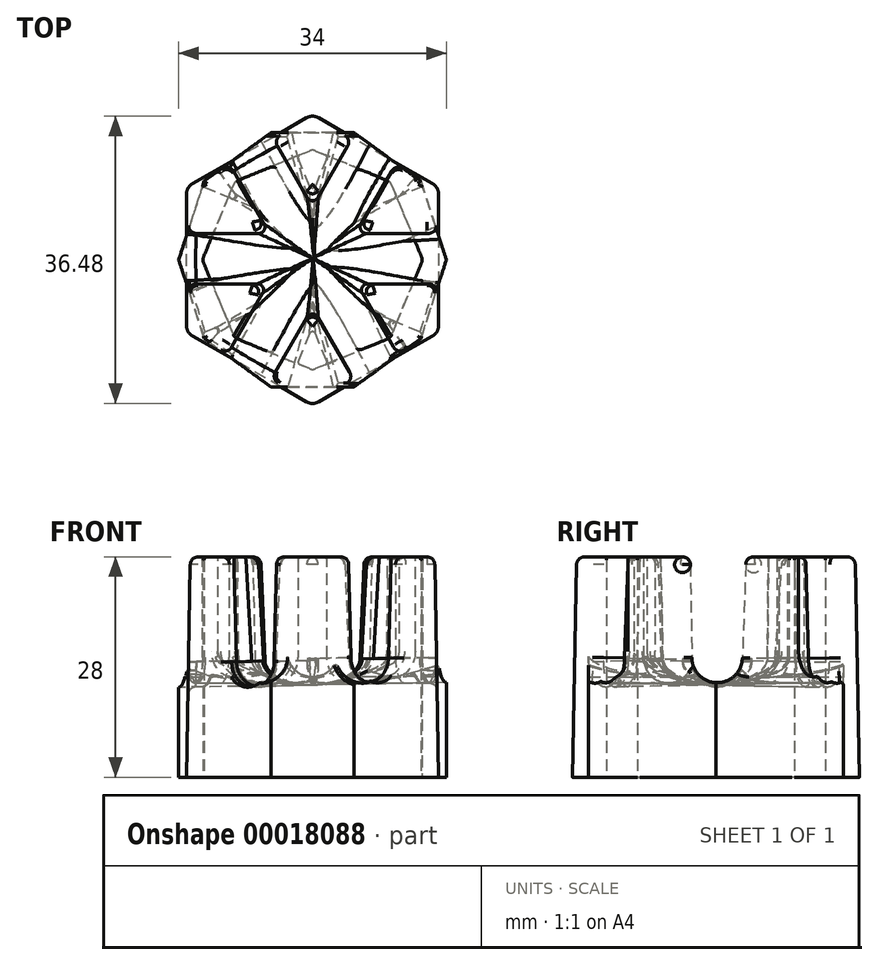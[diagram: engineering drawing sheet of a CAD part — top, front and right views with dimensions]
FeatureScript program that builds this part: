
annotation { "Feature Type Name" : "Feature", "Feature Type Description" : "" }
export const myFeature = defineFeature(function(context is Context, id is Id, definition is map)
    precondition{}
    {
        {
            var Q0;
            Q0=qCreatedBy(makeId("Top.planeOp"),FACE);
            var sketch = newSketch(context, id + "F0", { "sketchPlane" : qUnion([Q0])});
            skCircle(sketch, "E0.cCircle", {"center": v(0, 0) * mm, "radius": 17 * mm, "construction": true});
            skLineSegment(sketch, "E0.0", {"start": v(17, 0) * mm, "end": v(13.75, -10) * mm});
            skLineSegment(sketch, "E0.1", {"start": v(13.75, -10) * mm, "end": v(5.25, -16.17) * mm});
            skLineSegment(sketch, "E0.2", {"start": v(5.25, -16.17) * mm, "end": v(-5.25, -16.17) * mm});
            skLineSegment(sketch, "E0.3", {"start": v(-5.25, -16.17) * mm, "end": v(-13.75, -10) * mm});
            skLineSegment(sketch, "E0.4", {"start": v(-13.75, -10) * mm, "end": v(-17, 0) * mm});
            skLineSegment(sketch, "E0.5", {"start": v(-17, 0) * mm, "end": v(-13.75, 10) * mm});
            skLineSegment(sketch, "E0.6", {"start": v(-13.75, 10) * mm, "end": v(-5.25, 16.17) * mm});
            skLineSegment(sketch, "E0.7", {"start": v(-5.25, 16.17) * mm, "end": v(5.25, 16.17) * mm});
            skLineSegment(sketch, "E0.8", {"start": v(5.25, 16.17) * mm, "end": v(13.75, 10) * mm});
            skLineSegment(sketch, "E0.9", {"start": v(13.75, 10) * mm, "end": v(17, 0) * mm});
            skSolve(sketch);
        }
        {
            var Q0;
            Q0 = qSketchRegion(id + "F0", true);
            extrude(context, id + "F1", {"entities" : qUnion([Q0]), "depth" : 28 * mm});
        }
        {
            var Q0;
            Q0 = qSketchRegion(id + "F0", true);
            extrude(context, id + "F2", {"entities" : qUnion([Q0]), "operationType" : NewBodyOperationType.ADD, "depth" : 25 * mm});
        }
        {
            var Q0;
            Q0=makeQuery(id+"F1.opExtrude","SWEPT_FACE",FACE,{"disambiguationData":[OSD([sQuery(id+"F0.wireOp",EDGE,"E0.2")])]});
            var sketch = newSketch(context, id + "F3", { "sketchPlane" : qUnion([Q0])});
            skArc(sketch, "E1", {"start": v(-3.25, 16) * mm, "mid": v(0, 12.75) * mm, "end": v(3.25, 16) * mm});
            skLineSegment(sketch, "E2", {"start": v(-3.25, 28) * mm, "end": v(-3.25, 16) * mm});
            skLineSegment(sketch, "E3", {"start": v(3.25, 16) * mm, "end": v(3.25, 28) * mm});
            skLineSegment(sketch, "E4", {"start": v(3.25, 28) * mm, "end": v(-3.25, 28) * mm});
            skSolve(sketch);
        }
        {
            var Q0;
            Q0 = qSketchRegion(id + "F3", true);
            extrude(context, id + "F4", {"entities" : qUnion([Q0]), "depth" : 10 * mm, "hasSecondDirection" : true, "secondDirectionOppositeDirection" : true, "secondDirectionDepth" : 40 * mm});
        }
        {
            var Q0;
            Q0=qCreatedBy(makeId("Front.planeOp"),FACE);
            var sketch = newSketch(context, id + "F5", { "sketchPlane" : qUnion([Q0])});
            skLineSegment(sketch, "E5", {"start": v(0, 0) * mm, "end": v(0, 33.77) * mm});
            skSolve(sketch);
        }
        {
            var Q0;
            Q0=makeQuery(id+"F4.opExtrude","SWEPT_BODY",BODY,{"disambiguationData":[OSD([sQuery(id+"F3.wireOp",EDGE,"E1"),sQuery(id+"F3.wireOp",EDGE,"E2"),sQuery(id+"F3.wireOp",EDGE,"E3"),sQuery(id+"F3.wireOp",EDGE,"E4")])]});
            var Q1;
            Q1=sQuery(id+"F5.wireOp",EDGE,"E5");
            circularPattern(context, id + "F6", {"operationType" : NewBodyOperationType.REMOVE, "entities" : qUnion([Q0]), "axis" : qUnion([Q1]), "angle" : 35 * degree, "instanceCount" : 5});
        }
        {
            var Q0;
            Q0=qCreatedBy(makeId("Top.planeOp"),FACE);
            var sketch = newSketch(context, id + "F7", { "sketchPlane" : qUnion([Q0])});
            skCircle(sketch, "E6.cCircle", {"center": v(0, 0) * mm, "radius": 14 * mm, "construction": true});
            skLineSegment(sketch, "E6.0", {"start": v(14, 0) * mm, "end": v(9.9, -9.9) * mm});
            skLineSegment(sketch, "E6.1", {"start": v(9.9, -9.9) * mm, "end": v(0, -14) * mm});
            skLineSegment(sketch, "E6.2", {"start": v(0, -14) * mm, "end": v(-9.9, -9.9) * mm});
            skLineSegment(sketch, "E6.3", {"start": v(-9.9, -9.9) * mm, "end": v(-14, 0) * mm});
            skLineSegment(sketch, "E6.4", {"start": v(-14, 0) * mm, "end": v(-9.9, 9.9) * mm});
            skLineSegment(sketch, "E6.5", {"start": v(-9.9, 9.9) * mm, "end": v(0, 14) * mm});
            skLineSegment(sketch, "E6.6", {"start": v(0, 14) * mm, "end": v(9.9, 9.9) * mm});
            skLineSegment(sketch, "E6.7", {"start": v(9.9, 9.9) * mm, "end": v(14, 0) * mm});
            skSolve(sketch);
        }
        {
            var Q0;
            Q0=makeQuery(id+"F7.imprint","IMPRINT",FACE,{"disambiguationData":[TD([[makeQuery(id+"F7.imprint","IMPRINT",EDGE,{"derivedFrom":sQuery(id+"F7.wireOp",EDGE,"E6.0")}),-1.0]])]});
            extrude(context, id + "F8", {"entities" : qUnion([Q0]), "depth" : 28 * mm});
        }
        {
            var Q0;
            Q0=makeQuery(id+"F8.opExtrude","SWEPT_FACE",FACE,{"disambiguationData":[OSD([sQuery(id+"F7.wireOp",EDGE,"E6.1")])]});
            var sketch = newSketch(context, id + "F9", { "sketchPlane" : qUnion([Q0])});
            skLineSegment(sketch, "E7", {"start": v(0, 28) * mm, "end": v(0, 0) * mm, "construction": true});
            skArc(sketch, "E8", {"start": v(-3.25, 15.2) * mm, "mid": v(0, 11.95) * mm, "end": v(3.25, 15.2) * mm});
            skLineSegment(sketch, "E9", {"start": v(-3.25, 15.2) * mm, "end": v(-3.25, 28) * mm});
            skLineSegment(sketch, "E10", {"start": v(3.25, 15.2) * mm, "end": v(3.25, 28) * mm});
            skLineSegment(sketch, "E11", {"start": v(3.25, 28) * mm, "end": v(-3.25, 28) * mm});
            skSolve(sketch);
        }
        {
            var Q0;
            Q0 = qSketchRegion(id + "F9", true);
            extrude(context, id + "F10", {"entities" : qUnion([Q0]), "depth" : 25 * mm, "hasSecondDirection" : true, "secondDirectionOppositeDirection" : true, "secondDirectionDepth" : 34 * mm});
        }
        {
            var Q0;
            Q0=makeQuery(id+"F10.opExtrude","SWEPT_BODY",BODY,{"disambiguationData":[OSD([sQuery(id+"F9.wireOp",EDGE,"E8"),sQuery(id+"F9.wireOp",EDGE,"E9"),sQuery(id+"F9.wireOp",EDGE,"E10"),sQuery(id+"F9.wireOp",EDGE,"E11")])]});
            var Q1;
            Q1=sQuery(id+"F5.wireOp",EDGE,"E5");
            circularPattern(context, id + "F11", {"operationType" : NewBodyOperationType.REMOVE, "entities" : qUnion([Q0]), "axis" : qUnion([Q1]), "angle" : 45 * degree, "instanceCount" : 4});
        }
        {
            var Q0;
            Q0=makeQuery(id+"F8.opExtrude","SWEPT_EDGE",EDGE,{"disambiguationData":[OSD([sQuery(id+"F7.wireOp",EDGE,"E6.2"),sQuery(id+"F7.wireOp",EDGE,"E6.3")])]});
            var Q1;
            Q1=makeQuery(id+"F8.opExtrude","SWEPT_EDGE",EDGE,{"disambiguationData":[OSD([sQuery(id+"F7.wireOp",EDGE,"E6.1"),sQuery(id+"F7.wireOp",EDGE,"E6.2")])]});
            var Q2;
            Q2=makeQuery(id+"F8.opExtrude","SWEPT_EDGE",EDGE,{"disambiguationData":[OSD([sQuery(id+"F7.wireOp",EDGE,"E6.0"),sQuery(id+"F7.wireOp",EDGE,"E6.1")])]});
            var Q3;
            Q3=makeQuery(id+"F8.opExtrude","SWEPT_EDGE",EDGE,{"disambiguationData":[OSD([sQuery(id+"F7.wireOp",EDGE,"E6.0"),sQuery(id+"F7.wireOp",EDGE,"E6.7")])]});
            var Q4;
            Q4=makeQuery(id+"F8.opExtrude","SWEPT_EDGE",EDGE,{"disambiguationData":[OSD([sQuery(id+"F7.wireOp",EDGE,"E6.6"),sQuery(id+"F7.wireOp",EDGE,"E6.7")])]});
            var Q5;
            Q5=makeQuery(id+"F8.opExtrude","SWEPT_EDGE",EDGE,{"disambiguationData":[OSD([sQuery(id+"F7.wireOp",EDGE,"E6.5"),sQuery(id+"F7.wireOp",EDGE,"E6.6")])]});
            var Q6;
            Q6=makeQuery(id+"F8.opExtrude","SWEPT_EDGE",EDGE,{"disambiguationData":[OSD([sQuery(id+"F7.wireOp",EDGE,"E6.4"),sQuery(id+"F7.wireOp",EDGE,"E6.5")])]});
            var Q7;
            Q7=makeQuery(id+"F8.opExtrude","SWEPT_EDGE",EDGE,{"disambiguationData":[OSD([sQuery(id+"F7.wireOp",EDGE,"E6.3"),sQuery(id+"F7.wireOp",EDGE,"E6.4")])]});
            fillet(context, id + "F12", {"entities" : qUnion([Q0, Q1, Q2, Q3, Q4, Q5, Q6, Q7]), "radius" : 1 * mm, "tangentPropagation" : true, "allowEdgeOverflow" : false});
        }
        {
            var Q0;
            {var subQ0=sQuery(id+"F7.wireOp",EDGE,"E6.0");var subQ1=sQuery(id+"F7.wireOp",EDGE,"E6.1");Q0=makeQuery(id+"F11.boolean.opBoolean","SPLIT",FACE,{"disambiguationData":[TD([makeQuery(id+"F8.opExtrude","SWEPT_FACE",FACE,{"disambiguationData":[OSD([subQ0])]}),makeQuery(id+"F8.opExtrude","SWEPT_FACE",FACE,{"disambiguationData":[OSD([subQ1])]}),makeQuery(id+"F10.opExtrude","SWEPT_FACE",FACE,{"disambiguationData":[OSD([sQuery(id+"F9.wireOp",EDGE,"E10")])]}),makeQuery(id+"F11.opPattern","COPY",FACE,{"derivedFrom":makeQuery(id+"F10.opExtrude","SWEPT_FACE",FACE,{"disambiguationData":[OSD([sQuery(id+"F9.wireOp",EDGE,"E9")])]}),"instanceName":"1"})])],"derivedFrom":makeQuery(id+"F8.opExtrude","CAP_FACE",FACE,{"disambiguationData":[OSD([subQ0,subQ1,sQuery(id+"F7.wireOp",EDGE,"E6.2"),sQuery(id+"F7.wireOp",EDGE,"E6.3"),sQuery(id+"F7.wireOp",EDGE,"E6.4"),sQuery(id+"F7.wireOp",EDGE,"E6.5"),sQuery(id+"F7.wireOp",EDGE,"E6.6"),sQuery(id+"F7.wireOp",EDGE,"E6.7")])],"isStart":false})});}
            var Q1;
            {var subQ0=sQuery(id+"F7.wireOp",EDGE,"E6.0");var subQ1=sQuery(id+"F7.wireOp",EDGE,"E6.7");Q1=makeQuery(id+"F11.boolean.opBoolean","SPLIT",FACE,{"disambiguationData":[TD([makeQuery(id+"F8.opExtrude","SWEPT_FACE",FACE,{"disambiguationData":[OSD([subQ0])]}),makeQuery(id+"F8.opExtrude","SWEPT_FACE",FACE,{"disambiguationData":[OSD([subQ1])]}),makeQuery(id+"F11.opPattern","COPY",FACE,{"derivedFrom":makeQuery(id+"F10.opExtrude","SWEPT_FACE",FACE,{"disambiguationData":[OSD([sQuery(id+"F9.wireOp",EDGE,"E10")])]}),"instanceName":"1"}),makeQuery(id+"F11.opPattern","COPY",FACE,{"derivedFrom":makeQuery(id+"F10.opExtrude","SWEPT_FACE",FACE,{"disambiguationData":[OSD([sQuery(id+"F9.wireOp",EDGE,"E9")])]}),"instanceName":"2"})])],"derivedFrom":makeQuery(id+"F8.opExtrude","CAP_FACE",FACE,{"disambiguationData":[OSD([subQ0,sQuery(id+"F7.wireOp",EDGE,"E6.1"),sQuery(id+"F7.wireOp",EDGE,"E6.2"),sQuery(id+"F7.wireOp",EDGE,"E6.3"),sQuery(id+"F7.wireOp",EDGE,"E6.4"),sQuery(id+"F7.wireOp",EDGE,"E6.5"),sQuery(id+"F7.wireOp",EDGE,"E6.6"),subQ1])],"isStart":false})});}
            var Q2;
            {var subQ0=sQuery(id+"F7.wireOp",EDGE,"E6.6");var subQ1=sQuery(id+"F7.wireOp",EDGE,"E6.7");Q2=makeQuery(id+"F11.boolean.opBoolean","SPLIT",FACE,{"disambiguationData":[TD([makeQuery(id+"F8.opExtrude","SWEPT_FACE",FACE,{"disambiguationData":[OSD([subQ0])]}),makeQuery(id+"F8.opExtrude","SWEPT_FACE",FACE,{"disambiguationData":[OSD([subQ1])]}),makeQuery(id+"F11.opPattern","COPY",FACE,{"derivedFrom":makeQuery(id+"F10.opExtrude","SWEPT_FACE",FACE,{"disambiguationData":[OSD([sQuery(id+"F9.wireOp",EDGE,"E10")])]}),"instanceName":"2"}),makeQuery(id+"F11.opPattern","COPY",FACE,{"derivedFrom":makeQuery(id+"F10.opExtrude","SWEPT_FACE",FACE,{"disambiguationData":[OSD([sQuery(id+"F9.wireOp",EDGE,"E9")])]}),"instanceName":"3"})])],"derivedFrom":makeQuery(id+"F8.opExtrude","CAP_FACE",FACE,{"disambiguationData":[OSD([sQuery(id+"F7.wireOp",EDGE,"E6.0"),sQuery(id+"F7.wireOp",EDGE,"E6.1"),sQuery(id+"F7.wireOp",EDGE,"E6.2"),sQuery(id+"F7.wireOp",EDGE,"E6.3"),sQuery(id+"F7.wireOp",EDGE,"E6.4"),sQuery(id+"F7.wireOp",EDGE,"E6.5"),subQ0,subQ1])],"isStart":false})});}
            var Q3;
            {var subQ0=sQuery(id+"F7.wireOp",EDGE,"E6.5");var subQ1=sQuery(id+"F7.wireOp",EDGE,"E6.6");var subQ2=makeQuery(id+"F10.opExtrude","SWEPT_FACE",FACE,{"disambiguationData":[OSD([sQuery(id+"F9.wireOp",EDGE,"E10")])]});Q3=makeQuery(id+"F11.boolean.opBoolean","SPLIT",FACE,{"disambiguationData":[TD([makeQuery(id+"F8.opExtrude","SWEPT_FACE",FACE,{"disambiguationData":[OSD([subQ0])]}),makeQuery(id+"F8.opExtrude","SWEPT_FACE",FACE,{"disambiguationData":[OSD([subQ1])]}),subQ2,makeQuery(id+"F11.opPattern","COPY",FACE,{"derivedFrom":subQ2,"instanceName":"3"})])],"derivedFrom":makeQuery(id+"F8.opExtrude","CAP_FACE",FACE,{"disambiguationData":[OSD([sQuery(id+"F7.wireOp",EDGE,"E6.0"),sQuery(id+"F7.wireOp",EDGE,"E6.1"),sQuery(id+"F7.wireOp",EDGE,"E6.2"),sQuery(id+"F7.wireOp",EDGE,"E6.3"),sQuery(id+"F7.wireOp",EDGE,"E6.4"),subQ0,subQ1,sQuery(id+"F7.wireOp",EDGE,"E6.7")])],"isStart":false})});}
            var Q4;
            {var subQ0=sQuery(id+"F7.wireOp",EDGE,"E6.4");var subQ1=sQuery(id+"F7.wireOp",EDGE,"E6.5");Q4=makeQuery(id+"F11.boolean.opBoolean","SPLIT",FACE,{"disambiguationData":[TD([makeQuery(id+"F8.opExtrude","SWEPT_FACE",FACE,{"disambiguationData":[OSD([subQ0])]}),makeQuery(id+"F8.opExtrude","SWEPT_FACE",FACE,{"disambiguationData":[OSD([subQ1])]}),makeQuery(id+"F10.opExtrude","SWEPT_FACE",FACE,{"disambiguationData":[OSD([sQuery(id+"F9.wireOp",EDGE,"E9")])]}),makeQuery(id+"F11.opPattern","COPY",FACE,{"derivedFrom":makeQuery(id+"F10.opExtrude","SWEPT_FACE",FACE,{"disambiguationData":[OSD([sQuery(id+"F9.wireOp",EDGE,"E10")])]}),"instanceName":"1"})])],"derivedFrom":makeQuery(id+"F8.opExtrude","CAP_FACE",FACE,{"disambiguationData":[OSD([sQuery(id+"F7.wireOp",EDGE,"E6.0"),sQuery(id+"F7.wireOp",EDGE,"E6.1"),sQuery(id+"F7.wireOp",EDGE,"E6.2"),sQuery(id+"F7.wireOp",EDGE,"E6.3"),subQ0,subQ1,sQuery(id+"F7.wireOp",EDGE,"E6.6"),sQuery(id+"F7.wireOp",EDGE,"E6.7")])],"isStart":false})});}
            var Q5;
            {var subQ0=sQuery(id+"F7.wireOp",EDGE,"E6.3");var subQ1=sQuery(id+"F7.wireOp",EDGE,"E6.4");Q5=makeQuery(id+"F11.boolean.opBoolean","SPLIT",FACE,{"disambiguationData":[TD([makeQuery(id+"F8.opExtrude","SWEPT_FACE",FACE,{"disambiguationData":[OSD([subQ0])]}),makeQuery(id+"F8.opExtrude","SWEPT_FACE",FACE,{"disambiguationData":[OSD([subQ1])]}),makeQuery(id+"F11.opPattern","COPY",FACE,{"derivedFrom":makeQuery(id+"F10.opExtrude","SWEPT_FACE",FACE,{"disambiguationData":[OSD([sQuery(id+"F9.wireOp",EDGE,"E9")])]}),"instanceName":"1"}),makeQuery(id+"F11.opPattern","COPY",FACE,{"derivedFrom":makeQuery(id+"F10.opExtrude","SWEPT_FACE",FACE,{"disambiguationData":[OSD([sQuery(id+"F9.wireOp",EDGE,"E10")])]}),"instanceName":"2"})])],"derivedFrom":makeQuery(id+"F8.opExtrude","CAP_FACE",FACE,{"disambiguationData":[OSD([sQuery(id+"F7.wireOp",EDGE,"E6.0"),sQuery(id+"F7.wireOp",EDGE,"E6.1"),sQuery(id+"F7.wireOp",EDGE,"E6.2"),subQ0,subQ1,sQuery(id+"F7.wireOp",EDGE,"E6.5"),sQuery(id+"F7.wireOp",EDGE,"E6.6"),sQuery(id+"F7.wireOp",EDGE,"E6.7")])],"isStart":false})});}
            var Q6;
            {var subQ0=sQuery(id+"F7.wireOp",EDGE,"E6.2");var subQ1=sQuery(id+"F7.wireOp",EDGE,"E6.3");Q6=makeQuery(id+"F11.boolean.opBoolean","SPLIT",FACE,{"disambiguationData":[TD([makeQuery(id+"F8.opExtrude","SWEPT_FACE",FACE,{"disambiguationData":[OSD([subQ0])]}),makeQuery(id+"F8.opExtrude","SWEPT_FACE",FACE,{"disambiguationData":[OSD([subQ1])]}),makeQuery(id+"F11.opPattern","COPY",FACE,{"derivedFrom":makeQuery(id+"F10.opExtrude","SWEPT_FACE",FACE,{"disambiguationData":[OSD([sQuery(id+"F9.wireOp",EDGE,"E9")])]}),"instanceName":"2"}),makeQuery(id+"F11.opPattern","COPY",FACE,{"derivedFrom":makeQuery(id+"F10.opExtrude","SWEPT_FACE",FACE,{"disambiguationData":[OSD([sQuery(id+"F9.wireOp",EDGE,"E10")])]}),"instanceName":"3"})])],"derivedFrom":makeQuery(id+"F8.opExtrude","CAP_FACE",FACE,{"disambiguationData":[OSD([sQuery(id+"F7.wireOp",EDGE,"E6.0"),sQuery(id+"F7.wireOp",EDGE,"E6.1"),subQ0,subQ1,sQuery(id+"F7.wireOp",EDGE,"E6.4"),sQuery(id+"F7.wireOp",EDGE,"E6.5"),sQuery(id+"F7.wireOp",EDGE,"E6.6"),sQuery(id+"F7.wireOp",EDGE,"E6.7")])],"isStart":false})});}
            var Q7;
            {var subQ0=sQuery(id+"F7.wireOp",EDGE,"E6.1");var subQ1=sQuery(id+"F7.wireOp",EDGE,"E6.2");var subQ2=makeQuery(id+"F10.opExtrude","SWEPT_FACE",FACE,{"disambiguationData":[OSD([sQuery(id+"F9.wireOp",EDGE,"E9")])]});Q7=makeQuery(id+"F11.boolean.opBoolean","SPLIT",FACE,{"disambiguationData":[TD([makeQuery(id+"F8.opExtrude","SWEPT_FACE",FACE,{"disambiguationData":[OSD([subQ0])]}),makeQuery(id+"F8.opExtrude","SWEPT_FACE",FACE,{"disambiguationData":[OSD([subQ1])]}),subQ2,makeQuery(id+"F11.opPattern","COPY",FACE,{"derivedFrom":subQ2,"instanceName":"3"})])],"derivedFrom":makeQuery(id+"F8.opExtrude","CAP_FACE",FACE,{"disambiguationData":[OSD([sQuery(id+"F7.wireOp",EDGE,"E6.0"),subQ0,subQ1,sQuery(id+"F7.wireOp",EDGE,"E6.3"),sQuery(id+"F7.wireOp",EDGE,"E6.4"),sQuery(id+"F7.wireOp",EDGE,"E6.5"),sQuery(id+"F7.wireOp",EDGE,"E6.6"),sQuery(id+"F7.wireOp",EDGE,"E6.7")])],"isStart":false})});}
            var Q8;
            Q8=makeQuery(id+"F11.boolean.opBoolean","COPY",FACE,{"disambiguationData":[OD(0.0)],"derivedFrom":makeQuery(id+"F11.opPattern","COPY",FACE,{"derivedFrom":makeQuery(id+"F10.opExtrude","SWEPT_FACE",FACE,{"disambiguationData":[OSD([sQuery(id+"F9.wireOp",EDGE,"E10")])]}),"instanceName":"3"})});
            var Q9;
            Q9=makeQuery(id+"F11.boolean.opBoolean","COPY",FACE,{"disambiguationData":[OD(0.0)],"derivedFrom":makeQuery(id+"F11.opPattern","COPY",FACE,{"derivedFrom":makeQuery(id+"F10.opExtrude","SWEPT_FACE",FACE,{"disambiguationData":[OSD([sQuery(id+"F9.wireOp",EDGE,"E9")])]}),"instanceName":"1"})});
            var Q10;
            Q10=makeQuery(id+"F11.boolean.opBoolean","COPY",FACE,{"disambiguationData":[OD(0.0)],"derivedFrom":makeQuery(id+"F10.opExtrude","SWEPT_FACE",FACE,{"disambiguationData":[OSD([sQuery(id+"F9.wireOp",EDGE,"E9")])]})});
            var Q11;
            Q11=makeQuery(id+"F11.boolean.opBoolean","COPY",FACE,{"disambiguationData":[OD(1.0)],"derivedFrom":makeQuery(id+"F11.opPattern","COPY",FACE,{"derivedFrom":makeQuery(id+"F10.opExtrude","SWEPT_FACE",FACE,{"disambiguationData":[OSD([sQuery(id+"F9.wireOp",EDGE,"E9")])]}),"instanceName":"1"})});
            var Q12;
            Q12=makeQuery(id+"F11.boolean.opBoolean","COPY",FACE,{"disambiguationData":[OD(1.0)],"derivedFrom":makeQuery(id+"F10.opExtrude","SWEPT_FACE",FACE,{"disambiguationData":[OSD([sQuery(id+"F9.wireOp",EDGE,"E9")])]})});
            var Q13;
            Q13=makeQuery(id+"F11.boolean.opBoolean","COPY",FACE,{"disambiguationData":[OD(1.0)],"derivedFrom":makeQuery(id+"F11.opPattern","COPY",FACE,{"derivedFrom":makeQuery(id+"F10.opExtrude","SWEPT_FACE",FACE,{"disambiguationData":[OSD([sQuery(id+"F9.wireOp",EDGE,"E10")])]}),"instanceName":"3"})});
            var Q14;
            Q14=makeQuery(id+"F11.boolean.opBoolean","COPY",FACE,{"disambiguationData":[OD(1.0)],"derivedFrom":makeQuery(id+"F11.opPattern","COPY",FACE,{"derivedFrom":makeQuery(id+"F10.opExtrude","SWEPT_FACE",FACE,{"disambiguationData":[OSD([sQuery(id+"F9.wireOp",EDGE,"E9")])]}),"instanceName":"2"})});
            var Q15;
            Q15=makeQuery(id+"F11.boolean.opBoolean","COPY",FACE,{"disambiguationData":[OD(0.0)],"derivedFrom":makeQuery(id+"F10.opExtrude","SWEPT_FACE",FACE,{"disambiguationData":[OSD([sQuery(id+"F9.wireOp",EDGE,"E10")])]})});
            var Q16;
            Q16=makeQuery(id+"F11.boolean.opBoolean","COPY",FACE,{"disambiguationData":[OD(0.0)],"derivedFrom":makeQuery(id+"F11.opPattern","COPY",FACE,{"derivedFrom":makeQuery(id+"F10.opExtrude","SWEPT_FACE",FACE,{"disambiguationData":[OSD([sQuery(id+"F9.wireOp",EDGE,"E9")])]}),"instanceName":"2"})});
            fillet(context, id + "F13", {"entities" : qUnion([Q0, Q1, Q2, Q3, Q4, Q5, Q6, Q7, Q8, Q9, Q10, Q11, Q12, Q13, Q14, Q15, Q16]), "radius" : .4 * mm, "tangentPropagation" : true, "allowEdgeOverflow" : false});
        }
        {
            var Q0;
            {var subQ0=sQuery(id+"F0.wireOp",EDGE,"E0.8");var subQ1=sQuery(id+"F0.wireOp",EDGE,"E0.9");Q0=makeQuery(id+"F6.boolean.opBoolean","SPLIT",FACE,{"disambiguationData":[TD([makeQuery(id+"F1.opExtrude","SWEPT_FACE",FACE,{"disambiguationData":[OSD([subQ0])]}),makeQuery(id+"F1.opExtrude","SWEPT_FACE",FACE,{"disambiguationData":[OSD([subQ1])]}),makeQuery(id+"F6.opPattern","COPY",FACE,{"derivedFrom":makeQuery(id+"F4.opExtrude","SWEPT_FACE",FACE,{"disambiguationData":[OSD([sQuery(id+"F3.wireOp",EDGE,"E3")])]}),"instanceName":"3"}),makeQuery(id+"F6.opPattern","COPY",FACE,{"derivedFrom":makeQuery(id+"F4.opExtrude","SWEPT_FACE",FACE,{"disambiguationData":[OSD([sQuery(id+"F3.wireOp",EDGE,"E2")])]}),"instanceName":"4"})])],"derivedFrom":makeQuery(id+"F1.opExtrude","CAP_FACE",FACE,{"disambiguationData":[OSD([sQuery(id+"F0.wireOp",EDGE,"E0.0"),sQuery(id+"F0.wireOp",EDGE,"E0.1"),sQuery(id+"F0.wireOp",EDGE,"E0.2"),sQuery(id+"F0.wireOp",EDGE,"E0.3"),sQuery(id+"F0.wireOp",EDGE,"E0.4"),sQuery(id+"F0.wireOp",EDGE,"E0.5"),sQuery(id+"F0.wireOp",EDGE,"E0.6"),sQuery(id+"F0.wireOp",EDGE,"E0.7"),subQ0,subQ1])],"isStart":false})});}
            var Q1;
            {var subQ0=sQuery(id+"F0.wireOp",EDGE,"E0.7");var subQ1=sQuery(id+"F0.wireOp",EDGE,"E0.8");var subQ2=makeQuery(id+"F4.opExtrude","SWEPT_FACE",FACE,{"disambiguationData":[OSD([sQuery(id+"F3.wireOp",EDGE,"E3")])]});Q1=makeQuery(id+"F6.boolean.opBoolean","SPLIT",FACE,{"disambiguationData":[TD([makeQuery(id+"F1.opExtrude","SWEPT_FACE",FACE,{"disambiguationData":[OSD([subQ0])]}),makeQuery(id+"F1.opExtrude","SWEPT_FACE",FACE,{"disambiguationData":[OSD([subQ1])]}),subQ2,makeQuery(id+"F6.opPattern","COPY",FACE,{"derivedFrom":subQ2,"instanceName":"4"})])],"derivedFrom":makeQuery(id+"F1.opExtrude","CAP_FACE",FACE,{"disambiguationData":[OSD([sQuery(id+"F0.wireOp",EDGE,"E0.0"),sQuery(id+"F0.wireOp",EDGE,"E0.1"),sQuery(id+"F0.wireOp",EDGE,"E0.2"),sQuery(id+"F0.wireOp",EDGE,"E0.3"),sQuery(id+"F0.wireOp",EDGE,"E0.4"),sQuery(id+"F0.wireOp",EDGE,"E0.5"),sQuery(id+"F0.wireOp",EDGE,"E0.6"),subQ0,subQ1,sQuery(id+"F0.wireOp",EDGE,"E0.9")])],"isStart":false})});}
            var Q2;
            {var subQ0=sQuery(id+"F0.wireOp",EDGE,"E0.6");var subQ1=sQuery(id+"F0.wireOp",EDGE,"E0.7");Q2=makeQuery(id+"F6.boolean.opBoolean","SPLIT",FACE,{"disambiguationData":[TD([makeQuery(id+"F1.opExtrude","SWEPT_FACE",FACE,{"disambiguationData":[OSD([subQ0])]}),makeQuery(id+"F1.opExtrude","SWEPT_FACE",FACE,{"disambiguationData":[OSD([subQ1])]}),makeQuery(id+"F4.opExtrude","SWEPT_FACE",FACE,{"disambiguationData":[OSD([sQuery(id+"F3.wireOp",EDGE,"E2")])]}),makeQuery(id+"F6.opPattern","COPY",FACE,{"derivedFrom":makeQuery(id+"F4.opExtrude","SWEPT_FACE",FACE,{"disambiguationData":[OSD([sQuery(id+"F3.wireOp",EDGE,"E3")])]}),"instanceName":"1"})])],"derivedFrom":makeQuery(id+"F1.opExtrude","CAP_FACE",FACE,{"disambiguationData":[OSD([sQuery(id+"F0.wireOp",EDGE,"E0.0"),sQuery(id+"F0.wireOp",EDGE,"E0.1"),sQuery(id+"F0.wireOp",EDGE,"E0.2"),sQuery(id+"F0.wireOp",EDGE,"E0.3"),sQuery(id+"F0.wireOp",EDGE,"E0.4"),sQuery(id+"F0.wireOp",EDGE,"E0.5"),subQ0,subQ1,sQuery(id+"F0.wireOp",EDGE,"E0.8"),sQuery(id+"F0.wireOp",EDGE,"E0.9")])],"isStart":false})});}
            var Q3;
            {var subQ0=sQuery(id+"F0.wireOp",EDGE,"E0.5");var subQ1=sQuery(id+"F0.wireOp",EDGE,"E0.6");Q3=makeQuery(id+"F6.boolean.opBoolean","SPLIT",FACE,{"disambiguationData":[TD([makeQuery(id+"F1.opExtrude","SWEPT_FACE",FACE,{"disambiguationData":[OSD([subQ0])]}),makeQuery(id+"F1.opExtrude","SWEPT_FACE",FACE,{"disambiguationData":[OSD([subQ1])]}),makeQuery(id+"F6.opPattern","COPY",FACE,{"derivedFrom":makeQuery(id+"F4.opExtrude","SWEPT_FACE",FACE,{"disambiguationData":[OSD([sQuery(id+"F3.wireOp",EDGE,"E2")])]}),"instanceName":"1"}),makeQuery(id+"F6.opPattern","COPY",FACE,{"derivedFrom":makeQuery(id+"F4.opExtrude","SWEPT_FACE",FACE,{"disambiguationData":[OSD([sQuery(id+"F3.wireOp",EDGE,"E3")])]}),"instanceName":"2"})])],"derivedFrom":makeQuery(id+"F1.opExtrude","CAP_FACE",FACE,{"disambiguationData":[OSD([sQuery(id+"F0.wireOp",EDGE,"E0.0"),sQuery(id+"F0.wireOp",EDGE,"E0.1"),sQuery(id+"F0.wireOp",EDGE,"E0.2"),sQuery(id+"F0.wireOp",EDGE,"E0.3"),sQuery(id+"F0.wireOp",EDGE,"E0.4"),subQ0,subQ1,sQuery(id+"F0.wireOp",EDGE,"E0.7"),sQuery(id+"F0.wireOp",EDGE,"E0.8"),sQuery(id+"F0.wireOp",EDGE,"E0.9")])],"isStart":false})});}
            var Q4;
            {var subQ0=sQuery(id+"F0.wireOp",EDGE,"E0.4");var subQ1=sQuery(id+"F0.wireOp",EDGE,"E0.5");Q4=makeQuery(id+"F6.boolean.opBoolean","SPLIT",FACE,{"disambiguationData":[TD([makeQuery(id+"F1.opExtrude","SWEPT_FACE",FACE,{"disambiguationData":[OSD([subQ0])]}),makeQuery(id+"F1.opExtrude","SWEPT_FACE",FACE,{"disambiguationData":[OSD([subQ1])]}),makeQuery(id+"F6.opPattern","COPY",FACE,{"derivedFrom":makeQuery(id+"F4.opExtrude","SWEPT_FACE",FACE,{"disambiguationData":[OSD([sQuery(id+"F3.wireOp",EDGE,"E2")])]}),"instanceName":"2"}),makeQuery(id+"F6.opPattern","COPY",FACE,{"derivedFrom":makeQuery(id+"F4.opExtrude","SWEPT_FACE",FACE,{"disambiguationData":[OSD([sQuery(id+"F3.wireOp",EDGE,"E3")])]}),"instanceName":"3"})])],"derivedFrom":makeQuery(id+"F1.opExtrude","CAP_FACE",FACE,{"disambiguationData":[OSD([sQuery(id+"F0.wireOp",EDGE,"E0.0"),sQuery(id+"F0.wireOp",EDGE,"E0.1"),sQuery(id+"F0.wireOp",EDGE,"E0.2"),sQuery(id+"F0.wireOp",EDGE,"E0.3"),subQ0,subQ1,sQuery(id+"F0.wireOp",EDGE,"E0.6"),sQuery(id+"F0.wireOp",EDGE,"E0.7"),sQuery(id+"F0.wireOp",EDGE,"E0.8"),sQuery(id+"F0.wireOp",EDGE,"E0.9")])],"isStart":false})});}
            var Q5;
            {var subQ0=sQuery(id+"F0.wireOp",EDGE,"E0.3");var subQ1=sQuery(id+"F0.wireOp",EDGE,"E0.4");Q5=makeQuery(id+"F6.boolean.opBoolean","SPLIT",FACE,{"disambiguationData":[TD([makeQuery(id+"F1.opExtrude","SWEPT_FACE",FACE,{"disambiguationData":[OSD([subQ0])]}),makeQuery(id+"F1.opExtrude","SWEPT_FACE",FACE,{"disambiguationData":[OSD([subQ1])]}),makeQuery(id+"F6.opPattern","COPY",FACE,{"derivedFrom":makeQuery(id+"F4.opExtrude","SWEPT_FACE",FACE,{"disambiguationData":[OSD([sQuery(id+"F3.wireOp",EDGE,"E2")])]}),"instanceName":"3"}),makeQuery(id+"F6.opPattern","COPY",FACE,{"derivedFrom":makeQuery(id+"F4.opExtrude","SWEPT_FACE",FACE,{"disambiguationData":[OSD([sQuery(id+"F3.wireOp",EDGE,"E3")])]}),"instanceName":"4"})])],"derivedFrom":makeQuery(id+"F1.opExtrude","CAP_FACE",FACE,{"disambiguationData":[OSD([sQuery(id+"F0.wireOp",EDGE,"E0.0"),sQuery(id+"F0.wireOp",EDGE,"E0.1"),sQuery(id+"F0.wireOp",EDGE,"E0.2"),subQ0,subQ1,sQuery(id+"F0.wireOp",EDGE,"E0.5"),sQuery(id+"F0.wireOp",EDGE,"E0.6"),sQuery(id+"F0.wireOp",EDGE,"E0.7"),sQuery(id+"F0.wireOp",EDGE,"E0.8"),sQuery(id+"F0.wireOp",EDGE,"E0.9")])],"isStart":false})});}
            var Q6;
            {var subQ0=sQuery(id+"F0.wireOp",EDGE,"E0.2");var subQ1=sQuery(id+"F0.wireOp",EDGE,"E0.3");var subQ2=makeQuery(id+"F4.opExtrude","SWEPT_FACE",FACE,{"disambiguationData":[OSD([sQuery(id+"F3.wireOp",EDGE,"E2")])]});Q6=makeQuery(id+"F6.boolean.opBoolean","SPLIT",FACE,{"disambiguationData":[TD([makeQuery(id+"F1.opExtrude","SWEPT_FACE",FACE,{"disambiguationData":[OSD([subQ0])]}),makeQuery(id+"F1.opExtrude","SWEPT_FACE",FACE,{"disambiguationData":[OSD([subQ1])]}),subQ2,makeQuery(id+"F6.opPattern","COPY",FACE,{"derivedFrom":subQ2,"instanceName":"4"})])],"derivedFrom":makeQuery(id+"F1.opExtrude","CAP_FACE",FACE,{"disambiguationData":[OSD([sQuery(id+"F0.wireOp",EDGE,"E0.0"),sQuery(id+"F0.wireOp",EDGE,"E0.1"),subQ0,subQ1,sQuery(id+"F0.wireOp",EDGE,"E0.4"),sQuery(id+"F0.wireOp",EDGE,"E0.5"),sQuery(id+"F0.wireOp",EDGE,"E0.6"),sQuery(id+"F0.wireOp",EDGE,"E0.7"),sQuery(id+"F0.wireOp",EDGE,"E0.8"),sQuery(id+"F0.wireOp",EDGE,"E0.9")])],"isStart":false})});}
            var Q7;
            {var subQ0=sQuery(id+"F0.wireOp",EDGE,"E0.1");var subQ1=sQuery(id+"F0.wireOp",EDGE,"E0.2");Q7=makeQuery(id+"F6.boolean.opBoolean","SPLIT",FACE,{"disambiguationData":[TD([makeQuery(id+"F1.opExtrude","SWEPT_FACE",FACE,{"disambiguationData":[OSD([subQ0])]}),makeQuery(id+"F1.opExtrude","SWEPT_FACE",FACE,{"disambiguationData":[OSD([subQ1])]}),makeQuery(id+"F4.opExtrude","SWEPT_FACE",FACE,{"disambiguationData":[OSD([sQuery(id+"F3.wireOp",EDGE,"E3")])]}),makeQuery(id+"F6.opPattern","COPY",FACE,{"derivedFrom":makeQuery(id+"F4.opExtrude","SWEPT_FACE",FACE,{"disambiguationData":[OSD([sQuery(id+"F3.wireOp",EDGE,"E2")])]}),"instanceName":"1"})])],"derivedFrom":makeQuery(id+"F1.opExtrude","CAP_FACE",FACE,{"disambiguationData":[OSD([sQuery(id+"F0.wireOp",EDGE,"E0.0"),subQ0,subQ1,sQuery(id+"F0.wireOp",EDGE,"E0.3"),sQuery(id+"F0.wireOp",EDGE,"E0.4"),sQuery(id+"F0.wireOp",EDGE,"E0.5"),sQuery(id+"F0.wireOp",EDGE,"E0.6"),sQuery(id+"F0.wireOp",EDGE,"E0.7"),sQuery(id+"F0.wireOp",EDGE,"E0.8"),sQuery(id+"F0.wireOp",EDGE,"E0.9")])],"isStart":false})});}
            var Q8;
            {var subQ0=sQuery(id+"F0.wireOp",EDGE,"E0.0");var subQ1=sQuery(id+"F0.wireOp",EDGE,"E0.1");Q8=makeQuery(id+"F6.boolean.opBoolean","SPLIT",FACE,{"disambiguationData":[TD([makeQuery(id+"F1.opExtrude","SWEPT_FACE",FACE,{"disambiguationData":[OSD([subQ0])]}),makeQuery(id+"F1.opExtrude","SWEPT_FACE",FACE,{"disambiguationData":[OSD([subQ1])]}),makeQuery(id+"F6.opPattern","COPY",FACE,{"derivedFrom":makeQuery(id+"F4.opExtrude","SWEPT_FACE",FACE,{"disambiguationData":[OSD([sQuery(id+"F3.wireOp",EDGE,"E3")])]}),"instanceName":"1"}),makeQuery(id+"F6.opPattern","COPY",FACE,{"derivedFrom":makeQuery(id+"F4.opExtrude","SWEPT_FACE",FACE,{"disambiguationData":[OSD([sQuery(id+"F3.wireOp",EDGE,"E2")])]}),"instanceName":"2"})])],"derivedFrom":makeQuery(id+"F1.opExtrude","CAP_FACE",FACE,{"disambiguationData":[OSD([subQ0,subQ1,sQuery(id+"F0.wireOp",EDGE,"E0.2"),sQuery(id+"F0.wireOp",EDGE,"E0.3"),sQuery(id+"F0.wireOp",EDGE,"E0.4"),sQuery(id+"F0.wireOp",EDGE,"E0.5"),sQuery(id+"F0.wireOp",EDGE,"E0.6"),sQuery(id+"F0.wireOp",EDGE,"E0.7"),sQuery(id+"F0.wireOp",EDGE,"E0.8"),sQuery(id+"F0.wireOp",EDGE,"E0.9")])],"isStart":false})});}
            var Q9;
            {var subQ0=sQuery(id+"F0.wireOp",EDGE,"E0.0");var subQ1=sQuery(id+"F0.wireOp",EDGE,"E0.9");Q9=makeQuery(id+"F6.boolean.opBoolean","SPLIT",FACE,{"disambiguationData":[TD([makeQuery(id+"F1.opExtrude","SWEPT_FACE",FACE,{"disambiguationData":[OSD([subQ0])]}),makeQuery(id+"F1.opExtrude","SWEPT_FACE",FACE,{"disambiguationData":[OSD([subQ1])]}),makeQuery(id+"F6.opPattern","COPY",FACE,{"derivedFrom":makeQuery(id+"F4.opExtrude","SWEPT_FACE",FACE,{"disambiguationData":[OSD([sQuery(id+"F3.wireOp",EDGE,"E3")])]}),"instanceName":"2"}),makeQuery(id+"F6.opPattern","COPY",FACE,{"derivedFrom":makeQuery(id+"F4.opExtrude","SWEPT_FACE",FACE,{"disambiguationData":[OSD([sQuery(id+"F3.wireOp",EDGE,"E2")])]}),"instanceName":"3"})])],"derivedFrom":makeQuery(id+"F1.opExtrude","CAP_FACE",FACE,{"disambiguationData":[OSD([subQ0,sQuery(id+"F0.wireOp",EDGE,"E0.1"),sQuery(id+"F0.wireOp",EDGE,"E0.2"),sQuery(id+"F0.wireOp",EDGE,"E0.3"),sQuery(id+"F0.wireOp",EDGE,"E0.4"),sQuery(id+"F0.wireOp",EDGE,"E0.5"),sQuery(id+"F0.wireOp",EDGE,"E0.6"),sQuery(id+"F0.wireOp",EDGE,"E0.7"),sQuery(id+"F0.wireOp",EDGE,"E0.8"),subQ1])],"isStart":false})});}
            var Q10;
            Q10=makeQuery(id+"F6.boolean.opBoolean","COPY",FACE,{"disambiguationData":[OD(1.0)],"derivedFrom":makeQuery(id+"F6.opPattern","COPY",FACE,{"derivedFrom":makeQuery(id+"F4.opExtrude","SWEPT_FACE",FACE,{"disambiguationData":[OSD([sQuery(id+"F3.wireOp",EDGE,"E3")])]}),"instanceName":"3"})});
            var Q11;
            Q11=makeQuery(id+"F6.boolean.opBoolean","COPY",FACE,{"disambiguationData":[OD(1.0)],"derivedFrom":makeQuery(id+"F6.opPattern","COPY",FACE,{"derivedFrom":makeQuery(id+"F4.opExtrude","SWEPT_FACE",FACE,{"disambiguationData":[OSD([sQuery(id+"F3.wireOp",EDGE,"E3")])]}),"instanceName":"4"})});
            var Q12;
            Q12=makeQuery(id+"F6.boolean.opBoolean","COPY",FACE,{"disambiguationData":[OD(1.0)],"derivedFrom":makeQuery(id+"F4.opExtrude","SWEPT_FACE",FACE,{"disambiguationData":[OSD([sQuery(id+"F3.wireOp",EDGE,"E2")])]})});
            var Q13;
            Q13=makeQuery(id+"F6.boolean.opBoolean","COPY",FACE,{"disambiguationData":[OD(1.0)],"derivedFrom":makeQuery(id+"F6.opPattern","COPY",FACE,{"derivedFrom":makeQuery(id+"F4.opExtrude","SWEPT_FACE",FACE,{"disambiguationData":[OSD([sQuery(id+"F3.wireOp",EDGE,"E2")])]}),"instanceName":"1"})});
            var Q14;
            Q14=makeQuery(id+"F6.boolean.opBoolean","COPY",FACE,{"disambiguationData":[OD(0.0)],"derivedFrom":makeQuery(id+"F6.opPattern","COPY",FACE,{"derivedFrom":makeQuery(id+"F4.opExtrude","SWEPT_FACE",FACE,{"disambiguationData":[OSD([sQuery(id+"F3.wireOp",EDGE,"E3")])]}),"instanceName":"3"})});
            var Q15;
            Q15=makeQuery(id+"F6.boolean.opBoolean","COPY",FACE,{"disambiguationData":[OD(0.0)],"derivedFrom":makeQuery(id+"F6.opPattern","COPY",FACE,{"derivedFrom":makeQuery(id+"F4.opExtrude","SWEPT_FACE",FACE,{"disambiguationData":[OSD([sQuery(id+"F3.wireOp",EDGE,"E3")])]}),"instanceName":"4"})});
            var Q16;
            Q16=makeQuery(id+"F6.boolean.opBoolean","COPY",FACE,{"disambiguationData":[OD(0.0)],"derivedFrom":makeQuery(id+"F4.opExtrude","SWEPT_FACE",FACE,{"disambiguationData":[OSD([sQuery(id+"F3.wireOp",EDGE,"E2")])]})});
            var Q17;
            Q17=makeQuery(id+"F6.boolean.opBoolean","COPY",FACE,{"disambiguationData":[OD(0.0)],"derivedFrom":makeQuery(id+"F6.opPattern","COPY",FACE,{"derivedFrom":makeQuery(id+"F4.opExtrude","SWEPT_FACE",FACE,{"disambiguationData":[OSD([sQuery(id+"F3.wireOp",EDGE,"E2")])]}),"instanceName":"1"})});
            var Q18;
            Q18=makeQuery(id+"F6.boolean.opBoolean","COPY",FACE,{"disambiguationData":[OD(0.0)],"derivedFrom":makeQuery(id+"F6.opPattern","COPY",FACE,{"derivedFrom":makeQuery(id+"F4.opExtrude","SWEPT_FACE",FACE,{"disambiguationData":[OSD([sQuery(id+"F3.wireOp",EDGE,"E3")])]}),"instanceName":"2"})});
            var Q19;
            Q19=makeQuery(id+"F6.boolean.opBoolean","COPY",FACE,{"disambiguationData":[OD(1.0)],"derivedFrom":makeQuery(id+"F6.opPattern","COPY",FACE,{"derivedFrom":makeQuery(id+"F4.opExtrude","SWEPT_FACE",FACE,{"disambiguationData":[OSD([sQuery(id+"F3.wireOp",EDGE,"E2")])]}),"instanceName":"2"})});
            var Q20;
            Q20=makeQuery(id+"F6.boolean.opBoolean","COPY",FACE,{"disambiguationData":[OD(0.0)],"derivedFrom":makeQuery(id+"F6.opPattern","COPY",FACE,{"derivedFrom":makeQuery(id+"F4.opExtrude","SWEPT_FACE",FACE,{"disambiguationData":[OSD([sQuery(id+"F3.wireOp",EDGE,"E3")])]}),"instanceName":"1"})});
            fillet(context, id + "F14", {"entities" : qUnion([Q0, Q1, Q2, Q3, Q4, Q5, Q6, Q7, Q8, Q9, Q10, Q11, Q12, Q13, Q14, Q15, Q16, Q17, Q18, Q19, Q20]), "radius" : .4 * mm, "tangentPropagation" : true, "allowEdgeOverflow" : false});
        }
        {
            var Q0;
            Q0=qCreatedBy(makeId("Top.planeOp"),FACE);
            var sketch = newSketch(context, id + "F15", { "sketchPlane" : qUnion([Q0])});
            skCircle(sketch, "E12.cCircle", {"center": v(0, 0) * mm, "radius": 16 * mm, "construction": true});
            skLineSegment(sketch, "E12.0", {"start": v(16, 9.24) * mm, "end": v(16, -9.24) * mm});
            skLineSegment(sketch, "E12.1", {"start": v(16, -9.24) * mm, "end": v(0, -18.48) * mm});
            skLineSegment(sketch, "E12.2", {"start": v(0, -18.48) * mm, "end": v(-16, -9.24) * mm});
            skLineSegment(sketch, "E12.3", {"start": v(-16, -9.24) * mm, "end": v(-16, 9.24) * mm});
            skLineSegment(sketch, "E12.4", {"start": v(-16, 9.24) * mm, "end": v(0, 18.48) * mm});
            skLineSegment(sketch, "E12.5", {"start": v(0, 18.48) * mm, "end": v(16, 9.24) * mm});
            skPoint(sketch, "E12.0.midPoint", {"position": v(16, 0) * mm});
            skSolve(sketch);
        }
        {
            var Q0;
            Q0 = qSketchRegion(id + "F15", true);
            extrude(context, id + "F16", {"entities" : qUnion([Q0]), "depth" : 28 * mm, "hasDraft" : true, "draftAngle" : 1 * degree, "draftPullDirection" : true});
        }
        {
            var Q0;
            Q0=makeQuery(id+"F16.opExtrude","SWEPT_FACE",FACE,{"disambiguationData":[OSD([sQuery(id+"F15.wireOp",EDGE,"E12.1")])]});
            var sketch = newSketch(context, id + "F17", { "sketchPlane" : qUnion([Q0])});
            skCircle(sketch, "E13", {"center": v(0, 14.93) * mm, "radius": 3.2 * mm});
            skLineSegment(sketch, "E14", {"start": v(-3.2, 14.93) * mm, "end": v(-3.2, 27.7) * mm});
            skLineSegment(sketch, "E15", {"start": v(3.2, 14.93) * mm, "end": v(3.2, 27.76) * mm});
            skLineSegment(sketch, "E16", {"start": v(3.2, 27.76) * mm, "end": v(-3.2, 27.7) * mm});
            skLineSegment(sketch, "E17", {"start": v(-3.2, 14.93) * mm, "end": v(-3.59, 29.8) * mm});
            skLineSegment(sketch, "E18", {"start": v(-3.59, 29.8) * mm, "end": v(3.59, 29.8) * mm});
            skLineSegment(sketch, "E19", {"start": v(3.59, 29.8) * mm, "end": v(3.2, 14.93) * mm});
            skSolve(sketch);
        }
        {
            var Q0;
            Q0 = qSketchRegion(id + "F17", true);
            extrude(context, id + "F18", {"entities" : qUnion([Q0]), "depth" : 25 * mm, "hasSecondDirection" : true, "secondDirectionOppositeDirection" : true, "secondDirectionDepth" : 50 * mm});
        }
        {
            var Q0;
            Q0=makeQuery(id+"F18.opExtrude","SWEPT_BODY",BODY,{"disambiguationData":[OSD([sQuery(id+"F17.wireOp",EDGE,"E13"),sQuery(id+"F17.wireOp",EDGE,"E14"),sQuery(id+"F17.wireOp",EDGE,"E15"),sQuery(id+"F17.wireOp",EDGE,"E16")])]});
            var Q1;
            Q1=sQuery(id+"F5.wireOp",EDGE,"E5");
            circularPattern(context, id + "F19", {"operationType" : NewBodyOperationType.REMOVE, "entities" : qUnion([Q0]), "axis" : qUnion([Q1]), "angle" : 60 * degree, "instanceCount" : 3});
        }
        {
            var Q0;
            Q0=makeQuery(id+"F16.opExtrude","SWEPT_EDGE",EDGE,{"disambiguationData":[OSD([sQuery(id+"F15.wireOp",EDGE,"E12.1"),sQuery(id+"F15.wireOp",EDGE,"E12.2")])]});
            var Q1;
            Q1=makeQuery(id+"F16.opExtrude","SWEPT_EDGE",EDGE,{"disambiguationData":[OSD([sQuery(id+"F15.wireOp",EDGE,"E12.0"),sQuery(id+"F15.wireOp",EDGE,"E12.1")])]});
            var Q2;
            Q2=makeQuery(id+"F16.opExtrude","SWEPT_EDGE",EDGE,{"disambiguationData":[OSD([sQuery(id+"F15.wireOp",EDGE,"E12.0"),sQuery(id+"F15.wireOp",EDGE,"E12.5")])]});
            var Q3;
            Q3=makeQuery(id+"F16.opExtrude","SWEPT_EDGE",EDGE,{"disambiguationData":[OSD([sQuery(id+"F15.wireOp",EDGE,"E12.4"),sQuery(id+"F15.wireOp",EDGE,"E12.5")])]});
            var Q4;
            Q4=makeQuery(id+"F16.opExtrude","SWEPT_EDGE",EDGE,{"disambiguationData":[OSD([sQuery(id+"F15.wireOp",EDGE,"E12.3"),sQuery(id+"F15.wireOp",EDGE,"E12.4")])]});
            var Q5;
            Q5=makeQuery(id+"F16.opExtrude","SWEPT_EDGE",EDGE,{"disambiguationData":[OSD([sQuery(id+"F15.wireOp",EDGE,"E12.2"),sQuery(id+"F15.wireOp",EDGE,"E12.3")])]});
            fillet(context, id + "F20", {"entities" : qUnion([Q0, Q1, Q2, Q3, Q4, Q5]), "radius" : 1.5 * mm, "tangentPropagation" : true, "allowEdgeOverflow" : false});
        }
        {
            var Q0;
            {var subQ0=sQuery(id+"F15.wireOp",EDGE,"E12.2");var subQ1=sQuery(id+"F15.wireOp",EDGE,"E12.3");Q0=makeQuery(id+"F19.boolean.opBoolean","SPLIT",FACE,{"disambiguationData":[TD([makeQuery(id+"F16.opExtrude","SWEPT_FACE",FACE,{"disambiguationData":[OSD([subQ0])]}),makeQuery(id+"F16.opExtrude","SWEPT_FACE",FACE,{"disambiguationData":[OSD([subQ1])]}),makeQuery(id+"F19.opPattern","COPY",FACE,{"derivedFrom":makeQuery(id+"F18.opExtrude","SWEPT_FACE",FACE,{"disambiguationData":[OSD([sQuery(id+"F17.wireOp",EDGE,"E17")])]}),"instanceName":"1"}),makeQuery(id+"F19.opPattern","COPY",FACE,{"derivedFrom":makeQuery(id+"F18.opExtrude","SWEPT_FACE",FACE,{"disambiguationData":[OSD([sQuery(id+"F17.wireOp",EDGE,"E19")])]}),"instanceName":"2"})])],"derivedFrom":makeQuery(id+"F16.opExtrude","CAP_FACE",FACE,{"disambiguationData":[OSD([sQuery(id+"F15.wireOp",EDGE,"E12.0"),sQuery(id+"F15.wireOp",EDGE,"E12.1"),subQ0,subQ1,sQuery(id+"F15.wireOp",EDGE,"E12.4"),sQuery(id+"F15.wireOp",EDGE,"E12.5")])],"isStart":false})});}
            var Q1;
            {var subQ0=sQuery(id+"F15.wireOp",EDGE,"E12.3");var subQ1=sQuery(id+"F15.wireOp",EDGE,"E12.4");Q1=makeQuery(id+"F19.boolean.opBoolean","SPLIT",FACE,{"disambiguationData":[TD([makeQuery(id+"F16.opExtrude","SWEPT_FACE",FACE,{"disambiguationData":[OSD([subQ0])]}),makeQuery(id+"F16.opExtrude","SWEPT_FACE",FACE,{"disambiguationData":[OSD([subQ1])]}),makeQuery(id+"F18.opExtrude","SWEPT_FACE",FACE,{"disambiguationData":[OSD([sQuery(id+"F17.wireOp",EDGE,"E17")])]}),makeQuery(id+"F19.opPattern","COPY",FACE,{"derivedFrom":makeQuery(id+"F18.opExtrude","SWEPT_FACE",FACE,{"disambiguationData":[OSD([sQuery(id+"F17.wireOp",EDGE,"E19")])]}),"instanceName":"1"})])],"derivedFrom":makeQuery(id+"F16.opExtrude","CAP_FACE",FACE,{"disambiguationData":[OSD([sQuery(id+"F15.wireOp",EDGE,"E12.0"),sQuery(id+"F15.wireOp",EDGE,"E12.1"),sQuery(id+"F15.wireOp",EDGE,"E12.2"),subQ0,subQ1,sQuery(id+"F15.wireOp",EDGE,"E12.5")])],"isStart":false})});}
            var Q2;
            {var subQ0=sQuery(id+"F15.wireOp",EDGE,"E12.4");var subQ1=sQuery(id+"F15.wireOp",EDGE,"E12.5");var subQ2=makeQuery(id+"F18.opExtrude","SWEPT_FACE",FACE,{"disambiguationData":[OSD([sQuery(id+"F17.wireOp",EDGE,"E19")])]});Q2=makeQuery(id+"F19.boolean.opBoolean","SPLIT",FACE,{"disambiguationData":[TD([makeQuery(id+"F16.opExtrude","SWEPT_FACE",FACE,{"disambiguationData":[OSD([subQ0])]}),makeQuery(id+"F16.opExtrude","SWEPT_FACE",FACE,{"disambiguationData":[OSD([subQ1])]}),subQ2,makeQuery(id+"F19.opPattern","COPY",FACE,{"derivedFrom":subQ2,"instanceName":"2"})])],"derivedFrom":makeQuery(id+"F16.opExtrude","CAP_FACE",FACE,{"disambiguationData":[OSD([sQuery(id+"F15.wireOp",EDGE,"E12.0"),sQuery(id+"F15.wireOp",EDGE,"E12.1"),sQuery(id+"F15.wireOp",EDGE,"E12.2"),sQuery(id+"F15.wireOp",EDGE,"E12.3"),subQ0,subQ1])],"isStart":false})});}
            var Q3;
            {var subQ0=sQuery(id+"F15.wireOp",EDGE,"E12.0");var subQ1=sQuery(id+"F15.wireOp",EDGE,"E12.5");Q3=makeQuery(id+"F19.boolean.opBoolean","SPLIT",FACE,{"disambiguationData":[TD([makeQuery(id+"F16.opExtrude","SWEPT_FACE",FACE,{"disambiguationData":[OSD([subQ0])]}),makeQuery(id+"F16.opExtrude","SWEPT_FACE",FACE,{"disambiguationData":[OSD([subQ1])]}),makeQuery(id+"F19.opPattern","COPY",FACE,{"derivedFrom":makeQuery(id+"F18.opExtrude","SWEPT_FACE",FACE,{"disambiguationData":[OSD([sQuery(id+"F17.wireOp",EDGE,"E19")])]}),"instanceName":"1"}),makeQuery(id+"F19.opPattern","COPY",FACE,{"derivedFrom":makeQuery(id+"F18.opExtrude","SWEPT_FACE",FACE,{"disambiguationData":[OSD([sQuery(id+"F17.wireOp",EDGE,"E17")])]}),"instanceName":"2"})])],"derivedFrom":makeQuery(id+"F16.opExtrude","CAP_FACE",FACE,{"disambiguationData":[OSD([subQ0,sQuery(id+"F15.wireOp",EDGE,"E12.1"),sQuery(id+"F15.wireOp",EDGE,"E12.2"),sQuery(id+"F15.wireOp",EDGE,"E12.3"),sQuery(id+"F15.wireOp",EDGE,"E12.4"),subQ1])],"isStart":false})});}
            var Q4;
            {var subQ0=sQuery(id+"F15.wireOp",EDGE,"E12.0");var subQ1=sQuery(id+"F15.wireOp",EDGE,"E12.1");Q4=makeQuery(id+"F19.boolean.opBoolean","SPLIT",FACE,{"disambiguationData":[TD([makeQuery(id+"F16.opExtrude","SWEPT_FACE",FACE,{"disambiguationData":[OSD([subQ0])]}),makeQuery(id+"F16.opExtrude","SWEPT_FACE",FACE,{"disambiguationData":[OSD([subQ1])]}),makeQuery(id+"F18.opExtrude","SWEPT_FACE",FACE,{"disambiguationData":[OSD([sQuery(id+"F17.wireOp",EDGE,"E19")])]}),makeQuery(id+"F19.opPattern","COPY",FACE,{"derivedFrom":makeQuery(id+"F18.opExtrude","SWEPT_FACE",FACE,{"disambiguationData":[OSD([sQuery(id+"F17.wireOp",EDGE,"E17")])]}),"instanceName":"1"})])],"derivedFrom":makeQuery(id+"F16.opExtrude","CAP_FACE",FACE,{"disambiguationData":[OSD([subQ0,subQ1,sQuery(id+"F15.wireOp",EDGE,"E12.2"),sQuery(id+"F15.wireOp",EDGE,"E12.3"),sQuery(id+"F15.wireOp",EDGE,"E12.4"),sQuery(id+"F15.wireOp",EDGE,"E12.5")])],"isStart":false})});}
            var Q5;
            {var subQ0=sQuery(id+"F15.wireOp",EDGE,"E12.1");var subQ1=sQuery(id+"F15.wireOp",EDGE,"E12.2");var subQ2=makeQuery(id+"F18.opExtrude","SWEPT_FACE",FACE,{"disambiguationData":[OSD([sQuery(id+"F17.wireOp",EDGE,"E17")])]});Q5=makeQuery(id+"F19.boolean.opBoolean","SPLIT",FACE,{"disambiguationData":[TD([makeQuery(id+"F16.opExtrude","SWEPT_FACE",FACE,{"disambiguationData":[OSD([subQ0])]}),makeQuery(id+"F16.opExtrude","SWEPT_FACE",FACE,{"disambiguationData":[OSD([subQ1])]}),subQ2,makeQuery(id+"F19.opPattern","COPY",FACE,{"derivedFrom":subQ2,"instanceName":"2"})])],"derivedFrom":makeQuery(id+"F16.opExtrude","CAP_FACE",FACE,{"disambiguationData":[OSD([sQuery(id+"F15.wireOp",EDGE,"E12.0"),subQ0,subQ1,sQuery(id+"F15.wireOp",EDGE,"E12.3"),sQuery(id+"F15.wireOp",EDGE,"E12.4"),sQuery(id+"F15.wireOp",EDGE,"E12.5")])],"isStart":false})});}
            var Q6;
            Q6=makeQuery(id+"F19.boolean.opBoolean","INTERSECT",EDGE,{"derivedFrom":[makeQuery(id+"F16.opExtrude","SWEPT_FACE",FACE,{"disambiguationData":[OSD([sQuery(id+"F15.wireOp",EDGE,"E12.2")])]}),makeQuery(id+"F19.opPattern","COPY",FACE,{"derivedFrom":makeQuery(id+"F18.opExtrude","SWEPT_FACE",FACE,{"disambiguationData":[OSD([sQuery(id+"F17.wireOp",EDGE,"E19")])]}),"instanceName":"2"})]});
            var Q7;
            Q7=makeQuery(id+"F19.boolean.opBoolean","INTERSECT",EDGE,{"derivedFrom":[makeQuery(id+"F16.opExtrude","SWEPT_FACE",FACE,{"disambiguationData":[OSD([sQuery(id+"F15.wireOp",EDGE,"E12.1")])]}),makeQuery(id+"F18.opExtrude","SWEPT_FACE",FACE,{"disambiguationData":[OSD([sQuery(id+"F17.wireOp",EDGE,"E19")])]})]});
            var Q8;
            Q8=makeQuery(id+"F19.boolean.opBoolean","INTERSECT",EDGE,{"derivedFrom":[makeQuery(id+"F16.opExtrude","SWEPT_FACE",FACE,{"disambiguationData":[OSD([sQuery(id+"F15.wireOp",EDGE,"E12.2")])]}),makeQuery(id+"F19.opPattern","COPY",FACE,{"derivedFrom":makeQuery(id+"F18.opExtrude","SWEPT_FACE",FACE,{"disambiguationData":[OSD([sQuery(id+"F17.wireOp",EDGE,"E17")])]}),"instanceName":"2"})]});
            var Q9;
            Q9=makeQuery(id+"F19.boolean.opBoolean","INTERSECT",EDGE,{"derivedFrom":[makeQuery(id+"F16.opExtrude","SWEPT_FACE",FACE,{"disambiguationData":[OSD([sQuery(id+"F15.wireOp",EDGE,"E12.3")])]}),makeQuery(id+"F19.opPattern","COPY",FACE,{"derivedFrom":makeQuery(id+"F18.opExtrude","SWEPT_FACE",FACE,{"disambiguationData":[OSD([sQuery(id+"F17.wireOp",EDGE,"E19")])]}),"instanceName":"1"})]});
            var Q10;
            Q10=makeQuery(id+"F19.boolean.opBoolean","INTERSECT",EDGE,{"derivedFrom":[makeQuery(id+"F16.opExtrude","SWEPT_FACE",FACE,{"disambiguationData":[OSD([sQuery(id+"F15.wireOp",EDGE,"E12.5")])]}),makeQuery(id+"F19.opPattern","COPY",FACE,{"derivedFrom":makeQuery(id+"F18.opExtrude","SWEPT_FACE",FACE,{"disambiguationData":[OSD([sQuery(id+"F17.wireOp",EDGE,"E17")])]}),"instanceName":"2"})]});
            var Q11;
            Q11=makeQuery(id+"F19.boolean.opBoolean","INTERSECT",EDGE,{"derivedFrom":[makeQuery(id+"F16.opExtrude","SWEPT_FACE",FACE,{"disambiguationData":[OSD([sQuery(id+"F15.wireOp",EDGE,"E12.3")])]}),makeQuery(id+"F19.opPattern","COPY",FACE,{"derivedFrom":makeQuery(id+"F18.opExtrude","SWEPT_FACE",FACE,{"disambiguationData":[OSD([sQuery(id+"F17.wireOp",EDGE,"E17")])]}),"instanceName":"1"})]});
            var Q12;
            Q12=makeQuery(id+"F19.boolean.opBoolean","INTERSECT",EDGE,{"derivedFrom":[makeQuery(id+"F16.opExtrude","SWEPT_FACE",FACE,{"disambiguationData":[OSD([sQuery(id+"F15.wireOp",EDGE,"E12.4")])]}),makeQuery(id+"F18.opExtrude","SWEPT_FACE",FACE,{"disambiguationData":[OSD([sQuery(id+"F17.wireOp",EDGE,"E19")])]})]});
            var Q13;
            Q13=makeQuery(id+"F19.boolean.opBoolean","INTERSECT",EDGE,{"derivedFrom":[makeQuery(id+"F16.opExtrude","SWEPT_FACE",FACE,{"disambiguationData":[OSD([sQuery(id+"F15.wireOp",EDGE,"E12.4")])]}),makeQuery(id+"F18.opExtrude","SWEPT_FACE",FACE,{"disambiguationData":[OSD([sQuery(id+"F17.wireOp",EDGE,"E17")])]})]});
            var Q14;
            Q14=makeQuery(id+"F19.boolean.opBoolean","INTERSECT",EDGE,{"derivedFrom":[makeQuery(id+"F16.opExtrude","SWEPT_FACE",FACE,{"disambiguationData":[OSD([sQuery(id+"F15.wireOp",EDGE,"E12.5")])]}),makeQuery(id+"F19.opPattern","COPY",FACE,{"derivedFrom":makeQuery(id+"F18.opExtrude","SWEPT_FACE",FACE,{"disambiguationData":[OSD([sQuery(id+"F17.wireOp",EDGE,"E19")])]}),"instanceName":"2"})]});
            var Q15;
            Q15=makeQuery(id+"F19.boolean.opBoolean","INTERSECT",EDGE,{"derivedFrom":[makeQuery(id+"F16.opExtrude","SWEPT_FACE",FACE,{"disambiguationData":[OSD([sQuery(id+"F15.wireOp",EDGE,"E12.0")])]}),makeQuery(id+"F19.opPattern","COPY",FACE,{"derivedFrom":makeQuery(id+"F18.opExtrude","SWEPT_FACE",FACE,{"disambiguationData":[OSD([sQuery(id+"F17.wireOp",EDGE,"E17")])]}),"instanceName":"1"})]});
            var Q16;
            Q16=makeQuery(id+"F19.boolean.opBoolean","INTERSECT",EDGE,{"derivedFrom":[makeQuery(id+"F16.opExtrude","SWEPT_FACE",FACE,{"disambiguationData":[OSD([sQuery(id+"F15.wireOp",EDGE,"E12.0")])]}),makeQuery(id+"F19.opPattern","COPY",FACE,{"derivedFrom":makeQuery(id+"F18.opExtrude","SWEPT_FACE",FACE,{"disambiguationData":[OSD([sQuery(id+"F17.wireOp",EDGE,"E19")])]}),"instanceName":"1"})]});
            var Q17;
            Q17=makeQuery(id+"F19.boolean.opBoolean","INTERSECT",EDGE,{"derivedFrom":[makeQuery(id+"F16.opExtrude","SWEPT_FACE",FACE,{"disambiguationData":[OSD([sQuery(id+"F15.wireOp",EDGE,"E12.1")])]}),makeQuery(id+"F18.opExtrude","SWEPT_FACE",FACE,{"disambiguationData":[OSD([sQuery(id+"F17.wireOp",EDGE,"E17")])]})]});
            fillet(context, id + "F21", {"entities" : qUnion([Q0, Q1, Q2, Q3, Q4, Q5, Q6, Q7, Q8, Q9, Q10, Q11, Q12, Q13, Q14, Q15, Q16, Q17]), "radius" : 1 * mm, "tangentPropagation" : true, "allowEdgeOverflow" : false});
        }
        {
            var Q0;
            Q0=makeQuery(id+"F19.boolean.opBoolean","INTERSECT",EDGE,{"derivedFrom":[makeQuery(id+"F18.opExtrude","SWEPT_FACE",FACE,{"disambiguationData":[OSD([sQuery(id+"F17.wireOp",EDGE,"E17")])]}),makeQuery(id+"F19.opPattern","COPY",FACE,{"derivedFrom":makeQuery(id+"F18.opExtrude","SWEPT_FACE",FACE,{"disambiguationData":[OSD([sQuery(id+"F17.wireOp",EDGE,"E19")])]}),"instanceName":"1"})]});
            var Q1;
            {var subQ0=makeQuery(id+"F18.opExtrude","SWEPT_FACE",FACE,{"disambiguationData":[OSD([sQuery(id+"F17.wireOp",EDGE,"E19")])]});Q1=makeQuery(id+"F19.boolean.opBoolean","INTERSECT",EDGE,{"derivedFrom":[subQ0,makeQuery(id+"F19.opPattern","COPY",FACE,{"derivedFrom":subQ0,"instanceName":"2"})]});}
            var Q2;
            Q2=makeQuery(id+"F19.boolean.opBoolean","INTERSECT",EDGE,{"derivedFrom":[makeQuery(id+"F19.opPattern","COPY",FACE,{"derivedFrom":makeQuery(id+"F18.opExtrude","SWEPT_FACE",FACE,{"disambiguationData":[OSD([sQuery(id+"F17.wireOp",EDGE,"E19")])]}),"instanceName":"1"}),makeQuery(id+"F19.opPattern","COPY",FACE,{"derivedFrom":makeQuery(id+"F18.opExtrude","SWEPT_FACE",FACE,{"disambiguationData":[OSD([sQuery(id+"F17.wireOp",EDGE,"E17")])]}),"instanceName":"2"})]});
            var Q3;
            {var subQ0=makeQuery(id+"F18.opExtrude","SWEPT_FACE",FACE,{"disambiguationData":[OSD([sQuery(id+"F17.wireOp",EDGE,"E17")])]});Q3=makeQuery(id+"F19.boolean.opBoolean","INTERSECT",EDGE,{"derivedFrom":[subQ0,makeQuery(id+"F19.opPattern","COPY",FACE,{"derivedFrom":subQ0,"instanceName":"2"})]});}
            fillet(context, id + "F22", {"entities" : qUnion([Q0, Q1, Q2, Q3]), "radius" : .8 * mm, "tangentPropagation" : true, "allowEdgeOverflow" : false});
        }
        {
            var Q0;
            Q0=makeQuery(id+"F19.boolean.opBoolean","INTERSECT",EDGE,{"derivedFrom":[makeQuery(id+"F19.opPattern","COPY",FACE,{"derivedFrom":makeQuery(id+"F18.opExtrude","SWEPT_FACE",FACE,{"disambiguationData":[OSD([sQuery(id+"F17.wireOp",EDGE,"E17")])]}),"instanceName":"1"}),makeQuery(id+"F19.opPattern","COPY",FACE,{"derivedFrom":makeQuery(id+"F18.opExtrude","SWEPT_FACE",FACE,{"disambiguationData":[OSD([sQuery(id+"F17.wireOp",EDGE,"E19")])]}),"instanceName":"2"})]});
            var Q1;
            Q1=makeQuery(id+"F19.boolean.opBoolean","INTERSECT",EDGE,{"derivedFrom":[makeQuery(id+"F18.opExtrude","SWEPT_FACE",FACE,{"disambiguationData":[OSD([sQuery(id+"F17.wireOp",EDGE,"E19")])]}),makeQuery(id+"F19.opPattern","COPY",FACE,{"derivedFrom":makeQuery(id+"F18.opExtrude","SWEPT_FACE",FACE,{"disambiguationData":[OSD([sQuery(id+"F17.wireOp",EDGE,"E17")])]}),"instanceName":"1"})]});
            fillet(context, id + "F23", {"entities" : qUnion([Q0, Q1]), "radius" : .8 * mm, "tangentPropagation" : true, "allowEdgeOverflow" : false});
        }
    });
